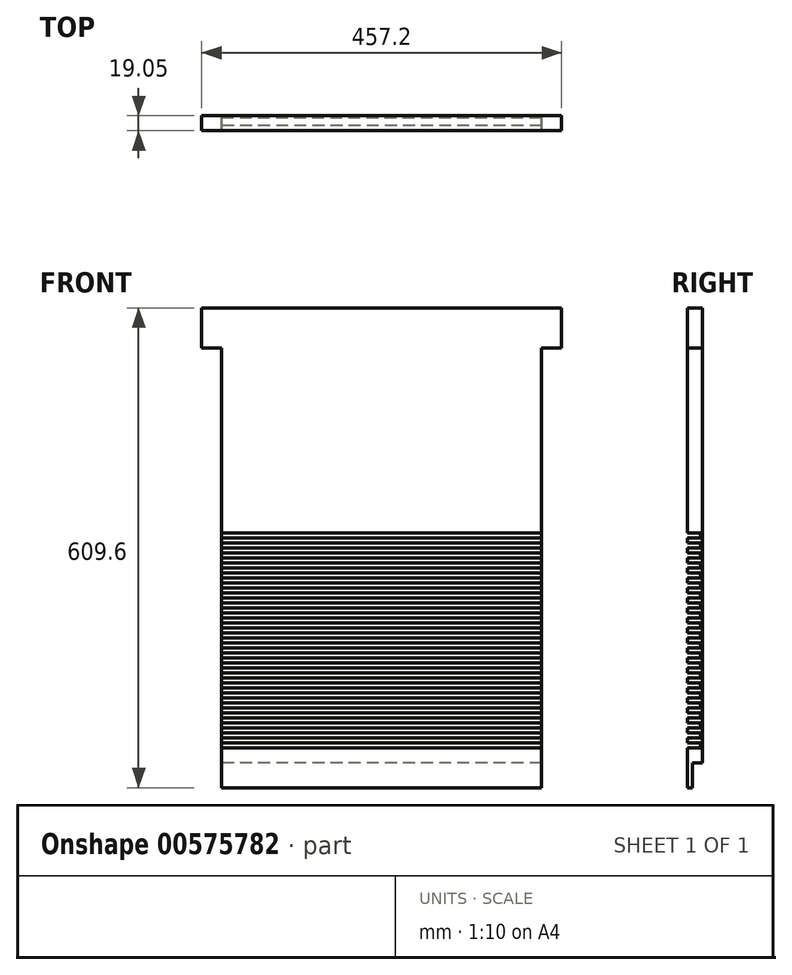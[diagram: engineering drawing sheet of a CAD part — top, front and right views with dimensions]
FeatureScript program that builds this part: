
annotation { "Feature Type Name" : "Feature", "Feature Type Description" : "" }
export const myFeature = defineFeature(function(context is Context, id is Id, definition is map)
    precondition{}
    {
        {
            var Q0;
            Q0=qCreatedBy(makeId("Front.planeOp"),FACE);
            var sketch = newSketch(context, id + "F0", { "sketchPlane" : qUnion([Q0])});
            skLineSegment(sketch, "E0", {"start": v(218.02, 487.6) * mm, "end": v(218.02, -71.2) * mm});
            skLineSegment(sketch, "E1", {"start": v(218.02, -71.2) * mm, "end": v(-188.38, -71.2) * mm});
            skLineSegment(sketch, "E2", {"start": v(-188.38, -71.2) * mm, "end": v(-188.38, 487.6) * mm});
            skLineSegment(sketch, "E3", {"start": v(-188.38, 487.6) * mm, "end": v(-213.78, 487.6) * mm});
            skLineSegment(sketch, "E4", {"start": v(-213.78, 487.6) * mm, "end": v(-213.78, 538.4) * mm});
            skLineSegment(sketch, "E5", {"start": v(-213.78, 538.4) * mm, "end": v(243.42, 538.4) * mm});
            skLineSegment(sketch, "E6", {"start": v(243.42, 538.4) * mm, "end": v(243.42, 487.6) * mm});
            skLineSegment(sketch, "E7", {"start": v(243.42, 487.6) * mm, "end": v(218.02, 487.6) * mm});
            skSolve(sketch);
        }
        {
            var Q0;
            Q0=qSketchRegion(id+"F0",true);
            extrude(context, id + "F1", {"entities" : qUnion([Q0]), "depth" : 19.05 * mm, "offsetDistance" : 25.4 * mm});
        }
        {
            var Q0;
            Q0=makeQuery(id+"F1.opExtrude","CAP_FACE",FACE,{"disambiguationData":[OSD([sQuery(id+"F0.wireOp",EDGE,"E0"),sQuery(id+"F0.wireOp",EDGE,"E1"),sQuery(id+"F0.wireOp",EDGE,"E2"),sQuery(id+"F0.wireOp",EDGE,"E3"),sQuery(id+"F0.wireOp",EDGE,"E4"),sQuery(id+"F0.wireOp",EDGE,"E5"),sQuery(id+"F0.wireOp",EDGE,"E6"),sQuery(id+"F0.wireOp",EDGE,"E7")])],"isStart":false});
            var sketch = newSketch(context, id + "F2", { "sketchPlane" : qUnion([Q0])});
            skLineSegment(sketch, "E8", {"start": v(-188.38, 259) * mm, "end": v(218.02, 259) * mm});
            skLineSegment(sketch, "E9", {"start": v(-188.38, -20.4) * mm, "end": v(218.02, -20.4) * mm});
            skLineSegment(sketch, "E10", {"start": v(-188.38, 246.3) * mm, "end": v(218.02, 246.3) * mm});
            skLineSegment(sketch, "E11", {"start": v(-188.38, 233.6) * mm, "end": v(218.02, 233.6) * mm});
            skLineSegment(sketch, "E12", {"start": v(-188.38, 239.95) * mm, "end": v(218.02, 239.95) * mm});
            skLineSegment(sketch, "E13", {"start": v(-188.38, 227.25) * mm, "end": v(218.02, 227.25) * mm});
            skLineSegment(sketch, "E14", {"start": v(-188.38, 252.65) * mm, "end": v(218.02, 252.65) * mm});
            skLineSegment(sketch, "E15", {"start": v(-188.38, 208.2) * mm, "end": v(218.02, 208.2) * mm});
            skLineSegment(sketch, "E16", {"start": v(-188.38, 201.85) * mm, "end": v(218.02, 201.85) * mm});
            skLineSegment(sketch, "E17", {"start": v(-188.38, 189.15) * mm, "end": v(218.02, 189.15) * mm});
            skLineSegment(sketch, "E18", {"start": v(-188.38, 182.8) * mm, "end": v(218.02, 182.8) * mm});
            skLineSegment(sketch, "E19", {"start": v(-188.38, 176.45) * mm, "end": v(218.02, 176.45) * mm});
            skLineSegment(sketch, "E20", {"start": v(-188.38, 170.1) * mm, "end": v(218.02, 170.1) * mm});
            skLineSegment(sketch, "E21", {"start": v(-188.38, 195.5) * mm, "end": v(218.02, 195.5) * mm});
            skLineSegment(sketch, "E22", {"start": v(-188.38, 214.55) * mm, "end": v(218.02, 214.55) * mm});
            skLineSegment(sketch, "E23", {"start": v(-188.38, 220.9) * mm, "end": v(218.02, 220.9) * mm});
            skLineSegment(sketch, "E24", {"start": v(-188.38, 93.9) * mm, "end": v(218.02, 93.9) * mm});
            skLineSegment(sketch, "E25", {"start": v(218.02, 74.85) * mm, "end": v(-188.38, 74.85) * mm});
            skLineSegment(sketch, "E26", {"start": v(-188.38, 62.15) * mm, "end": v(218.02, 62.15) * mm});
            skLineSegment(sketch, "E27", {"start": v(218.02, 49.45) * mm, "end": v(-188.38, 49.45) * mm});
            skLineSegment(sketch, "E28", {"start": v(-188.38, 43.1) * mm, "end": v(218.02, 43.1) * mm});
            skLineSegment(sketch, "E29", {"start": v(218.02, 30.4) * mm, "end": v(-188.38, 30.4) * mm});
            skLineSegment(sketch, "E30", {"start": v(-188.38, 17.7) * mm, "end": v(218.02, 17.7) * mm});
            skLineSegment(sketch, "E31", {"start": v(218.02, 11.35) * mm, "end": v(-188.38, 11.35) * mm});
            skLineSegment(sketch, "E32", {"start": v(-188.38, 5) * mm, "end": v(218.02, 5) * mm});
            skLineSegment(sketch, "E33", {"start": v(-188.38, 24.05) * mm, "end": v(218.02, 24.05) * mm});
            skLineSegment(sketch, "E34", {"start": v(-188.38, 87.55) * mm, "end": v(218.02, 87.55) * mm});
            skLineSegment(sketch, "E35", {"start": v(-188.38, 68.5) * mm, "end": v(218.02, 68.5) * mm});
            skLineSegment(sketch, "E36", {"start": v(-188.38, 81.2) * mm, "end": v(218.02, 81.2) * mm});
            skLineSegment(sketch, "E37", {"start": v(-188.38, 55.8) * mm, "end": v(218.02, 55.8) * mm});
            skLineSegment(sketch, "E38", {"start": v(-188.38, 36.75) * mm, "end": v(218.02, 36.75) * mm});
            skLineSegment(sketch, "E39", {"start": v(-188.38, -1.35) * mm, "end": v(218.02, -1.35) * mm});
            skLineSegment(sketch, "E40", {"start": v(-188.38, -14.05) * mm, "end": v(218.02, -14.05) * mm});
            skLineSegment(sketch, "E41", {"start": v(218.02, -7.7) * mm, "end": v(-188.38, -7.7) * mm});
            skLineSegment(sketch, "E42", {"start": v(-188.38, 100.25) * mm, "end": v(218.02, 100.25) * mm});
            skLineSegment(sketch, "E43", {"start": v(-188.38, 106.6) * mm, "end": v(218.02, 106.6) * mm});
            skLineSegment(sketch, "E44", {"start": v(-188.38, 112.95) * mm, "end": v(218.02, 112.95) * mm});
            skLineSegment(sketch, "E45", {"start": v(-188.38, 119.3) * mm, "end": v(218.02, 119.3) * mm});
            skLineSegment(sketch, "E46", {"start": v(-188.38, 125.65) * mm, "end": v(218.02, 125.65) * mm});
            skLineSegment(sketch, "E47", {"start": v(-188.38, 132) * mm, "end": v(218.02, 132) * mm});
            skLineSegment(sketch, "E48", {"start": v(-188.38, 138.35) * mm, "end": v(218.02, 138.35) * mm});
            skLineSegment(sketch, "E49", {"start": v(-188.38, 144.7) * mm, "end": v(218.02, 144.7) * mm});
            skLineSegment(sketch, "E50", {"start": v(-188.38, 151.05) * mm, "end": v(218.02, 151.05) * mm});
            skLineSegment(sketch, "E51", {"start": v(-188.38, 157.4) * mm, "end": v(218.02, 157.4) * mm});
            skLineSegment(sketch, "E52", {"start": v(-188.38, 163.75) * mm, "end": v(218.02, 163.75) * mm});
            skSolve(sketch);
        }
        {
            var Q0;
            {var subQ0=sQuery(id+"F2.wireOp",EDGE,"E9");Q0=makeQuery(id+"F2.imprint","IMPRINT",FACE,{"disambiguationData":[TD([[makeQuery(id+"F2.imprint","IMPRINT",EDGE,{"derivedFrom":subQ0}),1.0]])]});}
            var Q1;
            {var subQ0=sQuery(id+"F2.wireOp",EDGE,"E39");Q1=makeQuery(id+"F2.imprint","IMPRINT",FACE,{"disambiguationData":[TD([[makeQuery(id+"F2.imprint","IMPRINT",EDGE,{"derivedFrom":subQ0}),-1.0]])]});}
            var Q2;
            {var subQ0=sQuery(id+"F2.wireOp",EDGE,"E31");Q2=makeQuery(id+"F2.imprint","IMPRINT",FACE,{"disambiguationData":[TD([[makeQuery(id+"F2.imprint","IMPRINT",EDGE,{"derivedFrom":subQ0}),1.0]])]});}
            var Q3;
            {var subQ0=sQuery(id+"F2.wireOp",EDGE,"E30");Q3=makeQuery(id+"F2.imprint","IMPRINT",FACE,{"disambiguationData":[TD([[makeQuery(id+"F2.imprint","IMPRINT",EDGE,{"derivedFrom":subQ0}),1.0]])]});}
            var Q4;
            {var subQ0=sQuery(id+"F2.wireOp",EDGE,"E29");Q4=makeQuery(id+"F2.imprint","IMPRINT",FACE,{"disambiguationData":[TD([[makeQuery(id+"F2.imprint","IMPRINT",EDGE,{"derivedFrom":subQ0}),-1.0]])]});}
            var Q5;
            {var subQ0=sQuery(id+"F2.wireOp",EDGE,"E27");Q5=makeQuery(id+"F2.imprint","IMPRINT",FACE,{"disambiguationData":[TD([[makeQuery(id+"F2.imprint","IMPRINT",EDGE,{"derivedFrom":subQ0}),1.0]])]});}
            var Q6;
            {var subQ0=sQuery(id+"F2.wireOp",EDGE,"E26");Q6=makeQuery(id+"F2.imprint","IMPRINT",FACE,{"disambiguationData":[TD([[makeQuery(id+"F2.imprint","IMPRINT",EDGE,{"derivedFrom":subQ0}),-1.0]])]});}
            var Q7;
            {var subQ0=sQuery(id+"F2.wireOp",EDGE,"E25");Q7=makeQuery(id+"F2.imprint","IMPRINT",FACE,{"disambiguationData":[TD([[makeQuery(id+"F2.imprint","IMPRINT",EDGE,{"derivedFrom":subQ0}),1.0]])]});}
            var Q8;
            {var subQ0=sQuery(id+"F2.wireOp",EDGE,"E34");Q8=makeQuery(id+"F2.imprint","IMPRINT",FACE,{"disambiguationData":[TD([[makeQuery(id+"F2.imprint","IMPRINT",EDGE,{"derivedFrom":subQ0}),-1.0]])]});}
            var Q9;
            {var subQ0=sQuery(id+"F2.wireOp",EDGE,"E24");Q9=makeQuery(id+"F2.imprint","IMPRINT",FACE,{"disambiguationData":[TD([[makeQuery(id+"F2.imprint","IMPRINT",EDGE,{"derivedFrom":subQ0}),1.0]])]});}
            var Q10;
            {var subQ0=sQuery(id+"F2.wireOp",EDGE,"E43");Q10=makeQuery(id+"F2.imprint","IMPRINT",FACE,{"disambiguationData":[TD([[makeQuery(id+"F2.imprint","IMPRINT",EDGE,{"derivedFrom":subQ0}),1.0]])]});}
            var Q11;
            {var subQ0=sQuery(id+"F2.wireOp",EDGE,"E45");Q11=makeQuery(id+"F2.imprint","IMPRINT",FACE,{"disambiguationData":[TD([[makeQuery(id+"F2.imprint","IMPRINT",EDGE,{"derivedFrom":subQ0}),1.0]])]});}
            var Q12;
            {var subQ0=sQuery(id+"F2.wireOp",EDGE,"E47");Q12=makeQuery(id+"F2.imprint","IMPRINT",FACE,{"disambiguationData":[TD([[makeQuery(id+"F2.imprint","IMPRINT",EDGE,{"derivedFrom":subQ0}),1.0]])]});}
            var Q13;
            {var subQ0=sQuery(id+"F2.wireOp",EDGE,"E49");Q13=makeQuery(id+"F2.imprint","IMPRINT",FACE,{"disambiguationData":[TD([[makeQuery(id+"F2.imprint","IMPRINT",EDGE,{"derivedFrom":subQ0}),1.0]])]});}
            var Q14;
            {var subQ0=sQuery(id+"F2.wireOp",EDGE,"E51");Q14=makeQuery(id+"F2.imprint","IMPRINT",FACE,{"disambiguationData":[TD([[makeQuery(id+"F2.imprint","IMPRINT",EDGE,{"derivedFrom":subQ0}),1.0]])]});}
            var Q15;
            {var subQ0=sQuery(id+"F2.wireOp",EDGE,"E19");Q15=makeQuery(id+"F2.imprint","IMPRINT",FACE,{"disambiguationData":[TD([[makeQuery(id+"F2.imprint","IMPRINT",EDGE,{"derivedFrom":subQ0}),-1.0]])]});}
            var Q16;
            {var subQ0=sQuery(id+"F2.wireOp",EDGE,"E17");Q16=makeQuery(id+"F2.imprint","IMPRINT",FACE,{"disambiguationData":[TD([[makeQuery(id+"F2.imprint","IMPRINT",EDGE,{"derivedFrom":subQ0}),-1.0]])]});}
            var Q17;
            {var subQ0=sQuery(id+"F2.wireOp",EDGE,"E16");Q17=makeQuery(id+"F2.imprint","IMPRINT",FACE,{"disambiguationData":[TD([[makeQuery(id+"F2.imprint","IMPRINT",EDGE,{"derivedFrom":subQ0}),-1.0]])]});}
            var Q18;
            {var subQ0=sQuery(id+"F2.wireOp",EDGE,"E15");Q18=makeQuery(id+"F2.imprint","IMPRINT",FACE,{"disambiguationData":[TD([[makeQuery(id+"F2.imprint","IMPRINT",EDGE,{"derivedFrom":subQ0}),1.0]])]});}
            var Q19;
            {var subQ0=sQuery(id+"F2.wireOp",EDGE,"E13");Q19=makeQuery(id+"F2.imprint","IMPRINT",FACE,{"disambiguationData":[TD([[makeQuery(id+"F2.imprint","IMPRINT",EDGE,{"derivedFrom":subQ0}),-1.0]])]});}
            var Q20;
            {var subQ0=sQuery(id+"F2.wireOp",EDGE,"E11");Q20=makeQuery(id+"F2.imprint","IMPRINT",FACE,{"disambiguationData":[TD([[makeQuery(id+"F2.imprint","IMPRINT",EDGE,{"derivedFrom":subQ0}),1.0]])]});}
            var Q21;
            {var subQ0=sQuery(id+"F2.wireOp",EDGE,"E10");Q21=makeQuery(id+"F2.imprint","IMPRINT",FACE,{"disambiguationData":[TD([[makeQuery(id+"F2.imprint","IMPRINT",EDGE,{"derivedFrom":subQ0}),1.0]])]});}
            extrude(context, id + "F3", {"entities" : qUnion([Q0, Q1, Q2, Q3, Q4, Q5, Q6, Q7, Q8, Q9, Q10, Q11, Q12, Q13, Q14, Q15, Q16, Q17, Q18, Q19, Q20, Q21]), "operationType" : NewBodyOperationType.REMOVE, "oppositeDirection" : true, "depth" : 16.5 * mm, "offsetDistance" : 25.4 * mm});
        }
        {
            var Q0;
            Q0=makeQuery(id+"F1.opExtrude","CAP_FACE",FACE,{"disambiguationData":[OSD([sQuery(id+"F0.wireOp",EDGE,"E0"),sQuery(id+"F0.wireOp",EDGE,"E1"),sQuery(id+"F0.wireOp",EDGE,"E2"),sQuery(id+"F0.wireOp",EDGE,"E3"),sQuery(id+"F0.wireOp",EDGE,"E4"),sQuery(id+"F0.wireOp",EDGE,"E5"),sQuery(id+"F0.wireOp",EDGE,"E6"),sQuery(id+"F0.wireOp",EDGE,"E7")])],"isStart":true});
            var sketch = newSketch(context, id + "F4", { "sketchPlane" : qUnion([Q0])});
            skLineSegment(sketch, "E53", {"start": v(-218.02, -39.45) * mm, "end": v(188.38, -39.45) * mm});
            skSolve(sketch);
        }
        {
            var Q0;
            {var subQ0=sQuery(id+"F4.wireOp",EDGE,"E53");Q0=makeQuery(id+"F4.imprint","IMPRINT",FACE,{"disambiguationData":[TD([[makeQuery(id+"F4.imprint","IMPRINT",EDGE,{"derivedFrom":subQ0}),-1.0]])]});}
            extrude(context, id + "F5", {"entities" : qUnion([Q0]), "operationType" : NewBodyOperationType.REMOVE, "oppositeDirection" : true, "depth" : 12.7 * mm, "offsetDistance" : 25.4 * mm});
        }
    });
